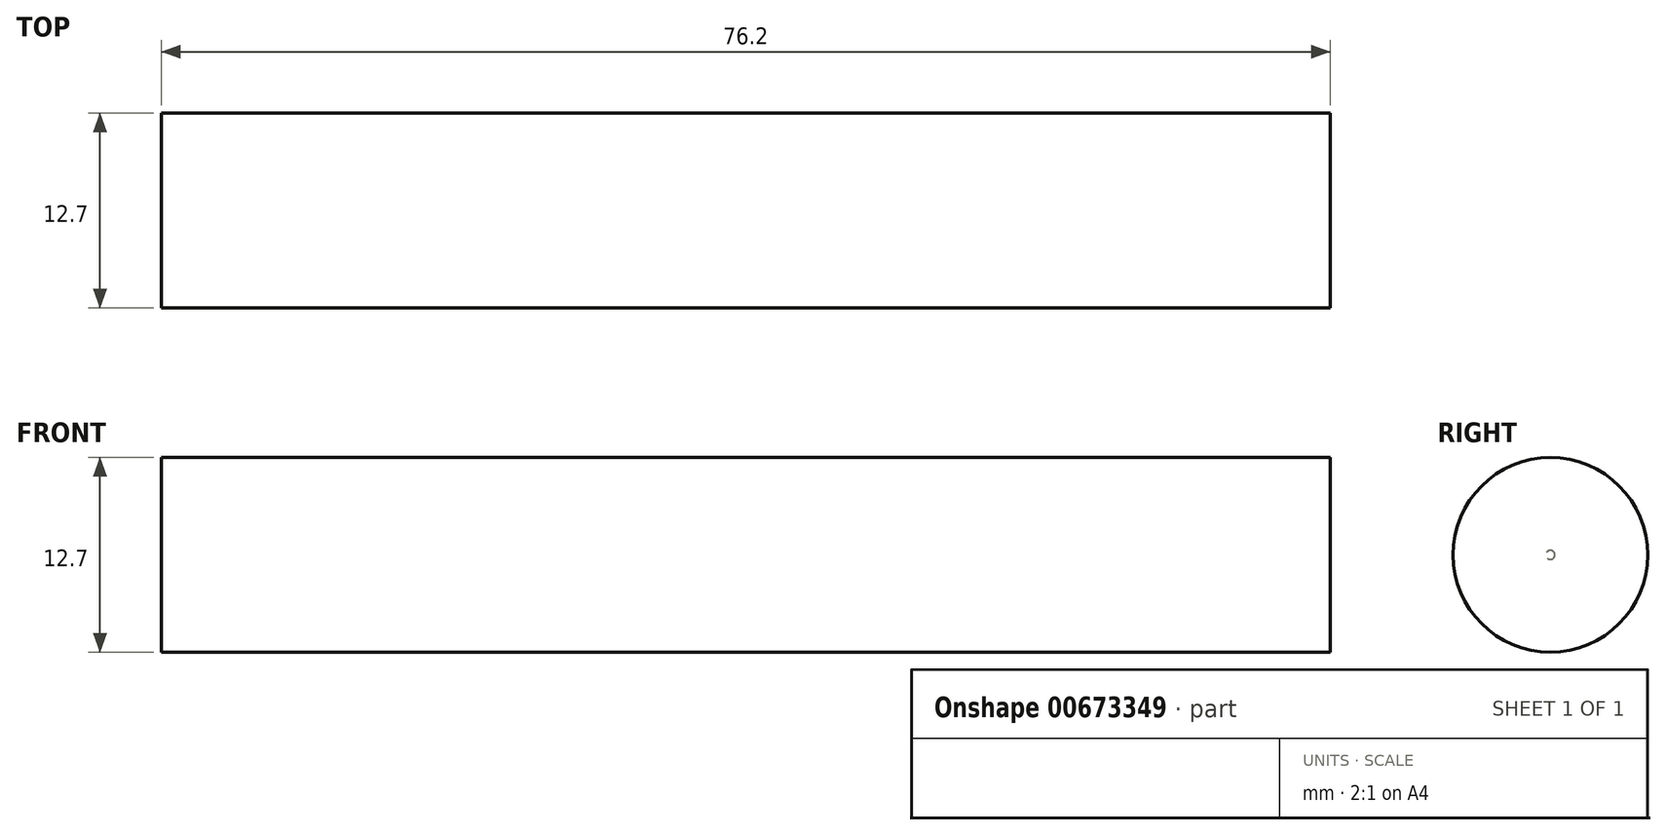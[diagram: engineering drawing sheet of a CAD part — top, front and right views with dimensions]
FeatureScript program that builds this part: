
annotation { "Feature Type Name" : "Feature", "Feature Type Description" : "" }
export const myFeature = defineFeature(function(context is Context, id is Id, definition is map)
    precondition{}
    {
        {
            var Q0;
            Q0=qCreatedBy(makeId("Top.planeOp"),FACE);
            var sketch = newSketch(context, id + "F0", { "sketchPlane" : qUnion([Q0])});
            skLineSegment(sketch, "E0", {"start": v(0, 0) * mm, "end": v(-19.05, 0) * mm});
            skCircle(sketch, "E1", {"center": v(-9.52, -0.15) * mm, "radius": 9.53 * mm});
            skPoint(sketch, "E1.third.point", {"position": v(-9.52, 9.38) * mm});
            skPoint(sketch, "E1.third.point.positionSnap0", {"position": v(-9.52, 0) * mm});
            skSolve(sketch);
        }
        {
            var Q0;
            {var subQ0=sQuery(id+"F0.wireOp",EDGE,"E0");Q0=makeQuery(id+"F0.imprint","IMPRINT",FACE,{"disambiguationData":[TD([[makeQuery(id+"F0.imprint","IMPRINT",EDGE,{"derivedFrom":subQ0}),1.0]])]});}
            var Q1;
            Q1=sQuery(id+"F0.wireOp",EDGE,"E0");
            revolve(context, id + "F1", {"entities" : qUnion([Q0]), "axis" : qUnion([Q1]), "revolveType" : RevolveType.FULL});
        }
        {
            var Q0;
            Q0=qCreatedBy(makeId("Right.planeOp"),FACE);
            var sketch = newSketch(context, id + "F2", { "sketchPlane" : qUnion([Q0])});
            skCircle(sketch, "E2", {"center": v(0, 0) * mm, "radius": 6.35 * mm});
            skSolve(sketch);
        }
        {
            var Q0;
            Q0 = qSketchRegion(id + "F2", true);
            extrude(context, id + "F3", {"entities" : qUnion([Q0]), "operationType" : NewBodyOperationType.ADD, "depth" : 76.2 * mm, "offsetDistance" : 25.4 * mm});
        }
    });
